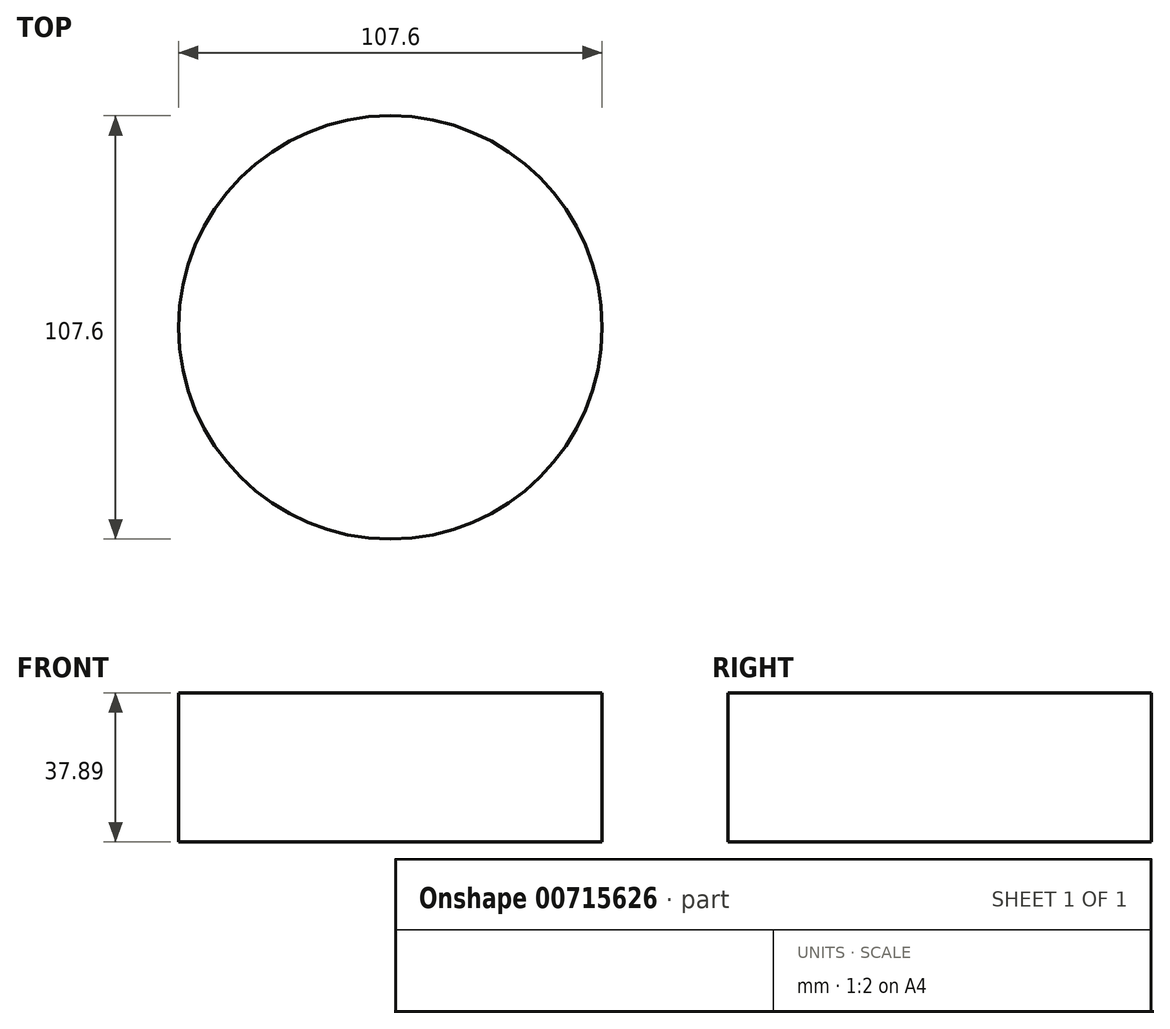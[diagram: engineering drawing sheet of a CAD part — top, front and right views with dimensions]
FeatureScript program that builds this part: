
annotation { "Feature Type Name" : "Feature", "Feature Type Description" : "" }
export const myFeature = defineFeature(function(context is Context, id is Id, definition is map)
    precondition{}
    {
        {
            var Q0;
            Q0=qCreatedBy(makeId("Top.planeOp"),FACE);
            var sketch = newSketch(context, id + "F0", { "sketchPlane" : qUnion([Q0])});
            skCircle(sketch, "E0", {"center": v(0, 0) * mm, "radius": 53.8 * mm});
            skSolve(sketch);
        }
        {
            var Q0;
            Q0=makeQuery(id+"F0.imprint","IMPRINT",FACE,{"disambiguationData":[TD([[makeQuery(id+"F0.imprint","IMPRINT",EDGE,{"derivedFrom":sQuery(id+"F0.wireOp",EDGE,"E0")}),1.0]])]});
            extrude(context, id + "F1", {"entities" : qUnion([Q0]), "depth" : 37.9 * mm, "offsetDistance" : 25.4 * mm});
        }
    });
